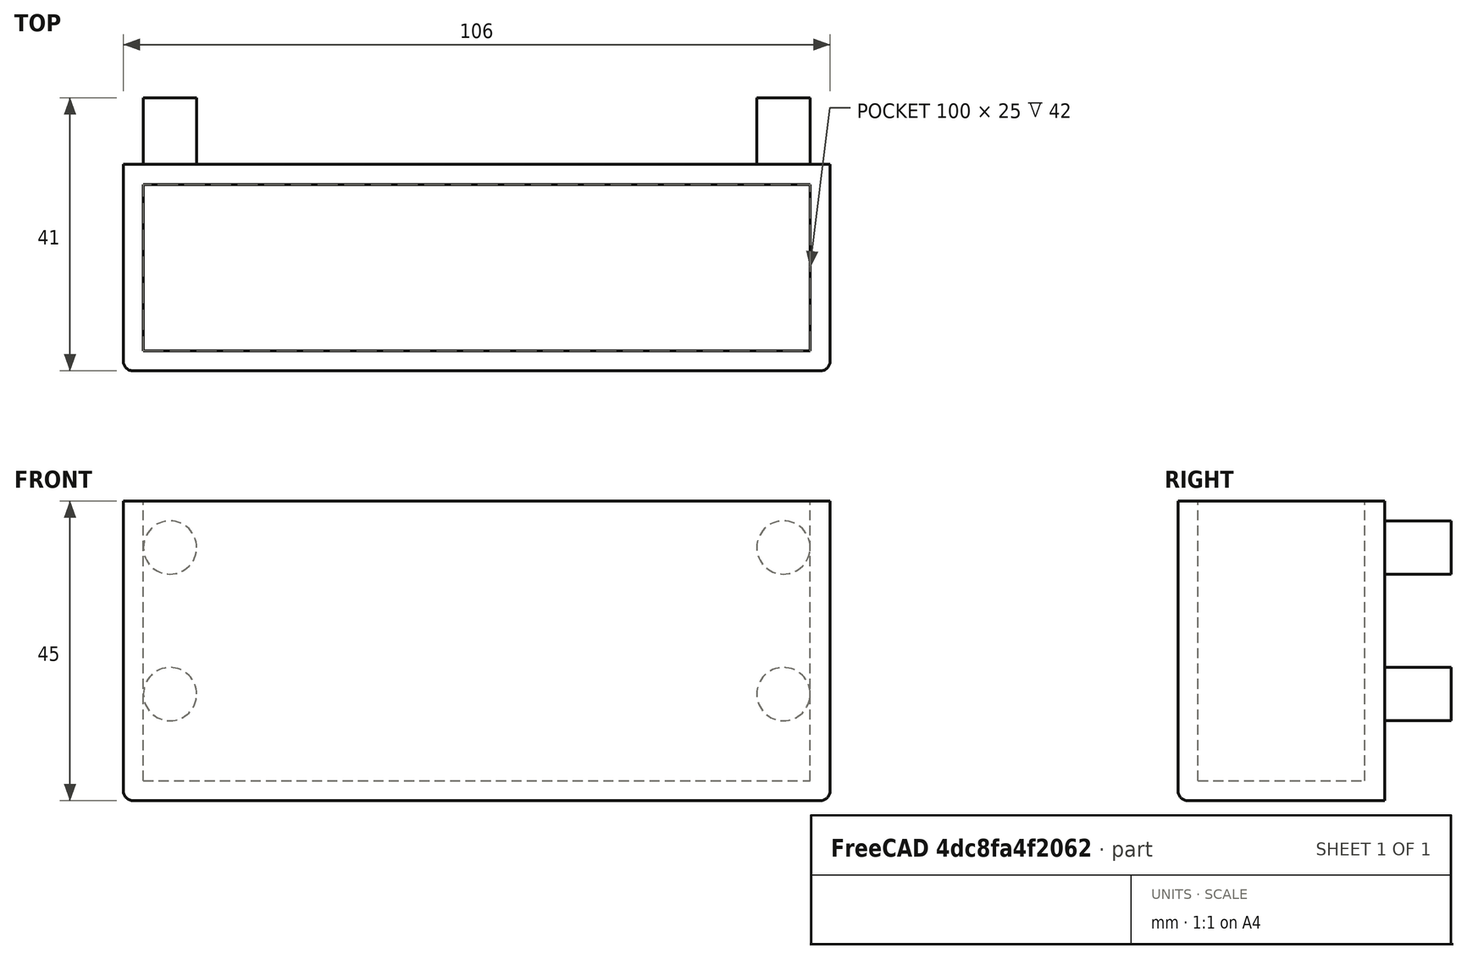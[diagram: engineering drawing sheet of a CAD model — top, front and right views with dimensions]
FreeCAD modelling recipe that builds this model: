
FCSTD DOCUMENT  (FreeCAD 0.15R4671 (Git))
Label: Holder_V6
License: All rights reserved
LicenseURL: http://en.wikipedia.org/wiki/All_rights_reserved
objects: Part::Cylinder×4, Part::Box×2, Part::Cut×1, Part::Fillet×1
note: 8 computed .brp shape members not serialized (recipe doc carries the construction recipe); baked Part::Feature solids carry a one-line shape summary decoded from their .brp

FEATURE [Part::Cylinder] Cylinder  label="Pin1"
  Angle = 360
  Height = 10
  Placement = pos=(0,0,0) rot=(1,0,0;1.5708rad)
  Radius = 4
FEATURE [Part::Cylinder] Cylinder001  label="Pin2"
  Angle = 360
  Height = 10
  Placement = pos=(92,0,0) rot=(1,0,0;1.5708rad)
  Radius = 4
FEATURE [Part::Box] Box  label="inside"
  Height = 42
  Length = 100
  Placement = pos=(-4,-38,-13) rot=(0,0,1;0rad)
  Width = 25
FEATURE [Part::Cylinder] Cylinder002  label="Pin3"
  Angle = 360
  Height = 10
  Placement = pos=(0,0,22) rot=(1,0,0;1.5708rad)
  Radius = 4
FEATURE [Part::Cylinder] Cylinder003  label="Pin4"
  Angle = 360
  Height = 10
  Placement = pos=(92,0,22) rot=(1,0,0;1.5708rad)
  Radius = 4
FEATURE [Part::Box] Box001  label="outside"
  Height = 45
  Length = 106
  Placement = pos=(-7,-41,-16) rot=(0,0,1;0rad)
  Width = 31
FEATURE [Part::Cut] Cut
  Base = -> Box001
  Tool = -> Box
FEATURE [Part::Fillet] Fillet
  Base = -> Cut
  Edges = 5 edges r=1.5: [Edge1,Edge4,Edge5,Edge6,Edge16]
